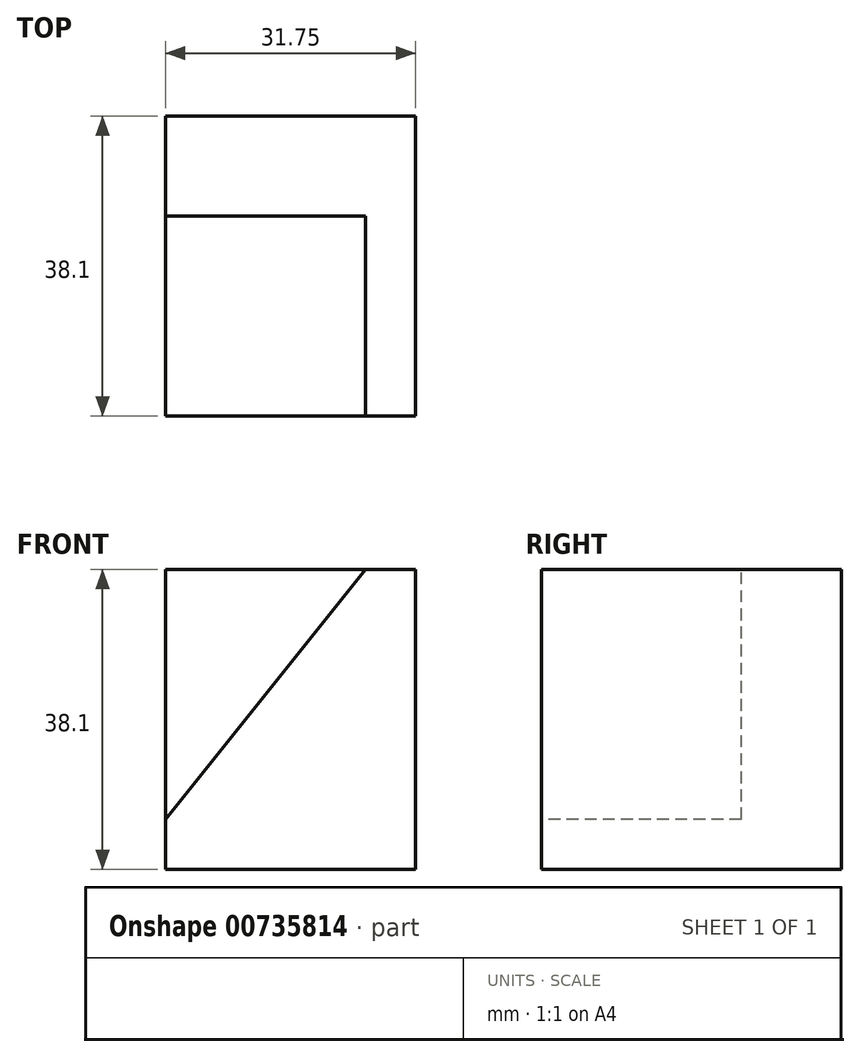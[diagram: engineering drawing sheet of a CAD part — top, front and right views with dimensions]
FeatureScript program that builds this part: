
annotation { "Feature Type Name" : "Feature", "Feature Type Description" : "" }
export const myFeature = defineFeature(function(context is Context, id is Id, definition is map)
    precondition{}
    {
        {
            var Q0;
            Q0=qCreatedBy(makeId("Front.planeOp"),FACE);
            var sketch = newSketch(context, id + "F0", { "sketchPlane" : qUnion([Q0])});
            skLineSegment(sketch, "E0", {"start": v(0, 0) * mm, "end": v(0, 38.1) * mm});
            skLineSegment(sketch, "E1", {"start": v(0, 38.1) * mm, "end": v(31.75, 38.1) * mm});
            skLineSegment(sketch, "E2", {"start": v(31.75, 38.1) * mm, "end": v(31.75, 0) * mm});
            skLineSegment(sketch, "E3", {"start": v(31.75, 0) * mm, "end": v(0, 0) * mm});
            skSolve(sketch);
        }
        {
            var Q0;
            Q0 = qSketchRegion(id + "F0", true);
            extrude(context, id + "F1", {"entities" : qUnion([Q0]), "depth" : 38.1 * mm, "offsetDistance" : 25.4 * mm});
        }
        {
            var Q0;
            Q0=makeQuery(id+"F1.opExtrude","CAP_FACE",FACE,{"disambiguationData":[OSD([sQuery(id+"F0.wireOp",EDGE,"E0"),sQuery(id+"F0.wireOp",EDGE,"E1"),sQuery(id+"F0.wireOp",EDGE,"E2"),sQuery(id+"F0.wireOp",EDGE,"E3")])],"isStart":false});
            var sketch = newSketch(context, id + "F2", { "sketchPlane" : qUnion([Q0])});
            skLineSegment(sketch, "E4", {"start": v(25.4, 38.1) * mm, "end": v(0, 6.35) * mm});
            skLineSegment(sketch, "E5", {"start": v(0, 6.35) * mm, "end": v(0, 38.1) * mm});
            skLineSegment(sketch, "E6", {"start": v(0, 38.1) * mm, "end": v(25.4, 38.1) * mm});
            skSolve(sketch);
        }
        {
            var Q0;
            Q0 = qSketchRegion(id + "F2", true);
            extrude(context, id + "F3", {"entities" : qUnion([Q0]), "operationType" : NewBodyOperationType.REMOVE, "oppositeDirection" : true, "depth" : 25.4 * mm, "offsetDistance" : 25.4 * mm});
        }
    });
